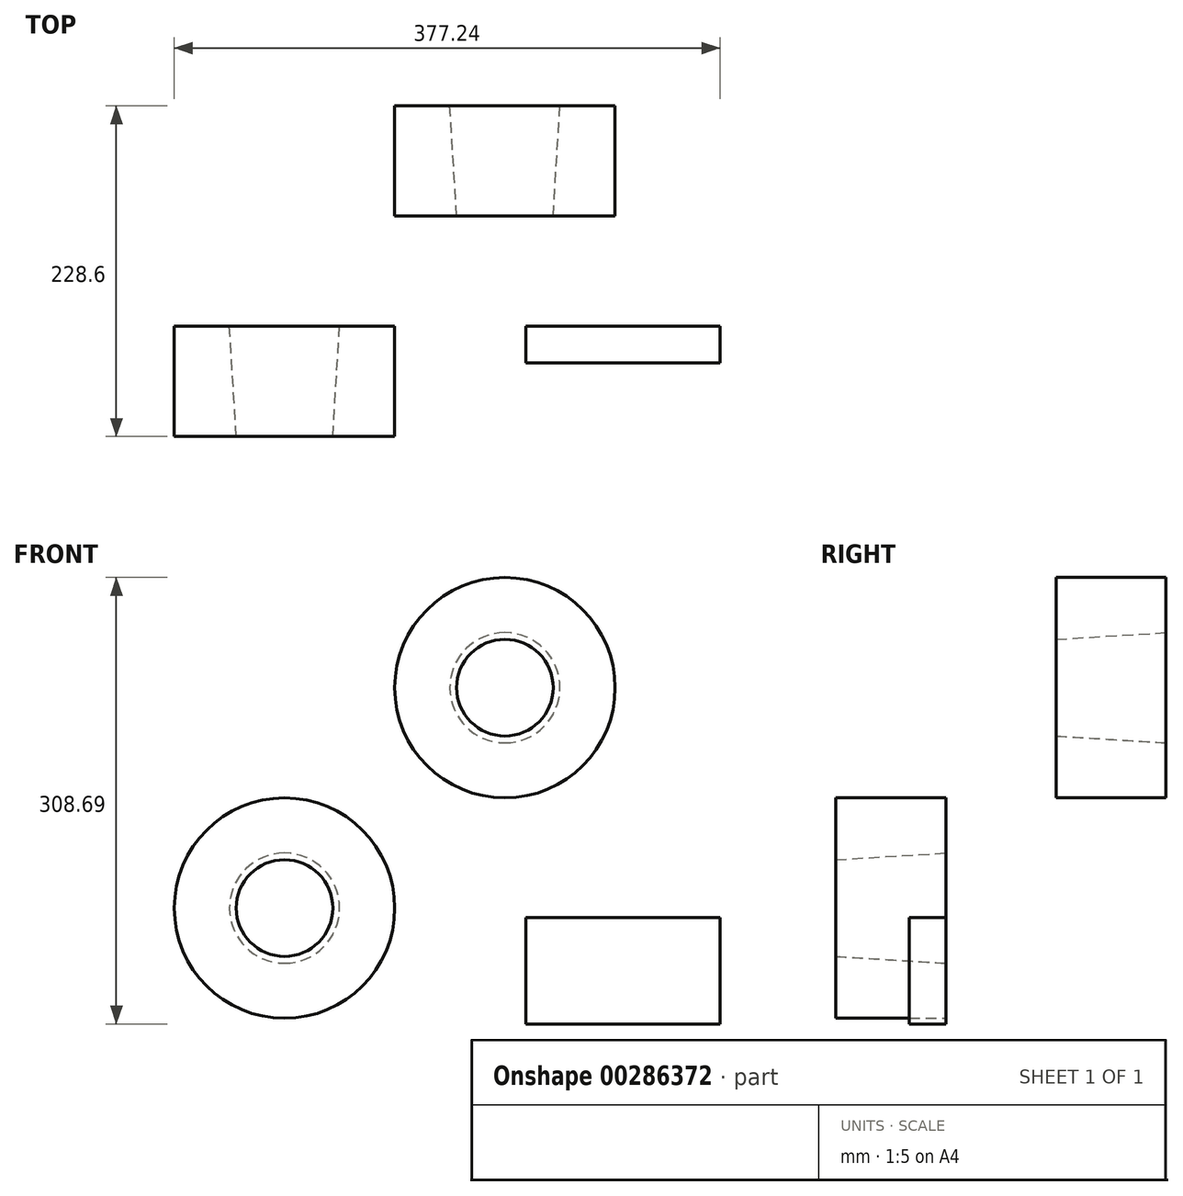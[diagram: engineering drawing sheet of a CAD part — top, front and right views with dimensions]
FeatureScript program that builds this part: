
annotation { "Feature Type Name" : "Feature", "Feature Type Description" : "" }
export const myFeature = defineFeature(function(context is Context, id is Id, definition is map)
    precondition{}
    {
        {
            var Q0;
            Q0=qCreatedBy(makeId("Front.planeOp"),FACE);
            var sketch = newSketch(context, id + "F0", { "sketchPlane" : qUnion([Q0])});
            skCircle(sketch, "E0", {"center": v(0, 0) * mm, "radius": 76.2 * mm});
            skSolve(sketch);
        }
        {
            var Q0;
            Q0=makeQuery(id+"F0.imprint","IMPRINT",FACE,{"disambiguationData":[TD([[makeQuery(id+"F0.imprint","IMPRINT",EDGE,{"derivedFrom":sQuery(id+"F0.wireOp",EDGE,"E0")}),1.0]])]});
            extrude(context, id + "F1", {"entities" : qUnion([Q0]), "depth" : 76.2 * mm});
        }
        {
            var Q0;
            Q0=makeQuery(id+"F1.opExtrude","CAP_FACE",FACE,{"disambiguationData":[OSD([sQuery(id+"F0.wireOp",EDGE,"E0")])],"isStart":true});
            var sketch = newSketch(context, id + "F2", { "sketchPlane" : qUnion([Q0])});
            skCircle(sketch, "E1", {"center": v(0, 0) * mm, "radius": 38.1 * mm});
            skSolve(sketch);
        }
        {
            var Q0;
            Q0=makeQuery(id+"F2.imprint","IMPRINT",FACE,{"disambiguationData":[TD([[makeQuery(id+"F2.imprint","IMPRINT",EDGE,{"derivedFrom":sQuery(id+"F2.wireOp",EDGE,"E1")}),1.0]])]});
            extrude(context, id + "F3", {"entities" : qUnion([Q0]), "operationType" : NewBodyOperationType.REMOVE, "endBound" : BoundingType.THROUGH_ALL, "oppositeDirection" : true, "depth" : 25.4 * mm, "hasDraft" : true, "draftAngle" : 3.54 * degree, "draftPullDirection" : true});
        }
        {
            var Q0;
            Q0=makeQuery(id+"F1.opExtrude","SWEPT_BODY",BODY,{"disambiguationData":[OSD([sQuery(id+"F0.wireOp",EDGE,"E0")])]});
            transform(context, id + "F4", {"entities" : qUnion([Q0]), "transformType" : TransformType.TRANSLATION_3D, "dx" : 152.4 * mm, "dy" : 152.4 * mm, "dz" : 152.4 * mm, "makeCopy" : true});
        }
        {
            var Q0;
            Q0=qCreatedBy(makeId("Front.planeOp"),FACE);
            var sketch = newSketch(context, id + "F5", { "sketchPlane" : qUnion([Q0])});
            skLineSegment(sketch, "E2.bottom", {"start": v(166.77, -6.7) * mm, "end": v(301.04, -6.7) * mm});
            skLineSegment(sketch, "E2.top", {"start": v(166.77, -80.1) * mm, "end": v(301.04, -80.1) * mm});
            skLineSegment(sketch, "E2.left", {"start": v(166.77, -6.7) * mm, "end": v(166.77, -80.1) * mm});
            skLineSegment(sketch, "E2.right", {"start": v(301.04, -6.7) * mm, "end": v(301.04, -80.1) * mm});
            skSolve(sketch);
        }
        {
            var Q0;
            Q0 = qSketchRegion(id + "F5", true);
            extrude(context, id + "F6", {"entities" : qUnion([Q0]), "depth" : 25.4 * mm});
        }
    });
